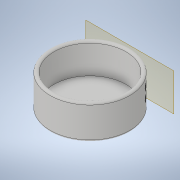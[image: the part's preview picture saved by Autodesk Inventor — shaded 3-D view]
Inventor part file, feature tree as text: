
AUTODESK INVENTOR PART (.ipt)
format: ipt  version: 2021.1 (Build 251245000, 245)  size: 782,336 bytes
history: native  units: in
note: dims shown in document units (in); Inventor stores cm internally (conversion verified against a paired STEP export)
features: extrude x2, fillet x2, sketch x2, plane x1, emboss x1
ambient origin geometry x8: Origin, YZ Plane, XZ Plane, XY Plane, X Axis, Y Axis, Z Axis, Center Point
bodies: Solid1 (feature_tree)
feature tree (8):
  extrude  "Extrusion1"  Depth=0.125in
  extrude  "Extrusion3"  Depth=0.0625in
  plane  "Work Plane1"
  emboss  "Emboss1"
  fillet  "Fillet1"  Radius=2.64in
  fillet  "Fillet2"  Radius=1.0in
  sketch  "Sketch1"  dims[d0=2.64in d2=0.125in]
  sketch  "Sketch5"  dims[d3=0.0in d4=2.39in d5=2.64in d9=1.0in d10=0.0in d11=0.05in d12=0.0in d13=0.0625in d14=0.0625in]
